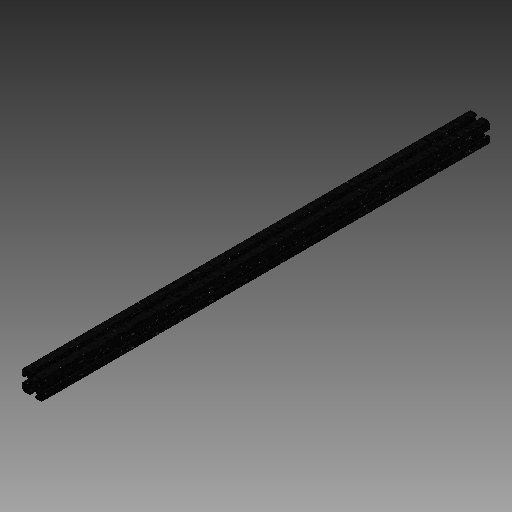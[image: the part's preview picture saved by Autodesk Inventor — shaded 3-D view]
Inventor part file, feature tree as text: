
AUTODESK INVENTOR PART (.ipt)
format: ipt  version: 2019 (Build 230136000, 136)  size: 249,856 bytes
history: native  units: in
note: dims shown in document units (in); Inventor stores cm internally (conversion verified against a paired STEP export)
features: plane x1, extrude x1, sketch x1
ambient origin geometry x8: Origin, YZ Plane, XZ Plane, XY Plane, X Axis, Y Axis, Z Axis, Center Point
bodies: Solid1 (feature_tree)
feature tree (3):
  plane  "Work Plane1"
  extrude  "Extrusion1"  [1 undecoded]
  sketch  "Sketch1"  dims[d0=12.0in d1=0.0in]
note: 1 required parameter value undecoded (feature->parameter linkage not recoverable at this tier; creation-order binding heuristic only, values carry confidence <= 0.55)
